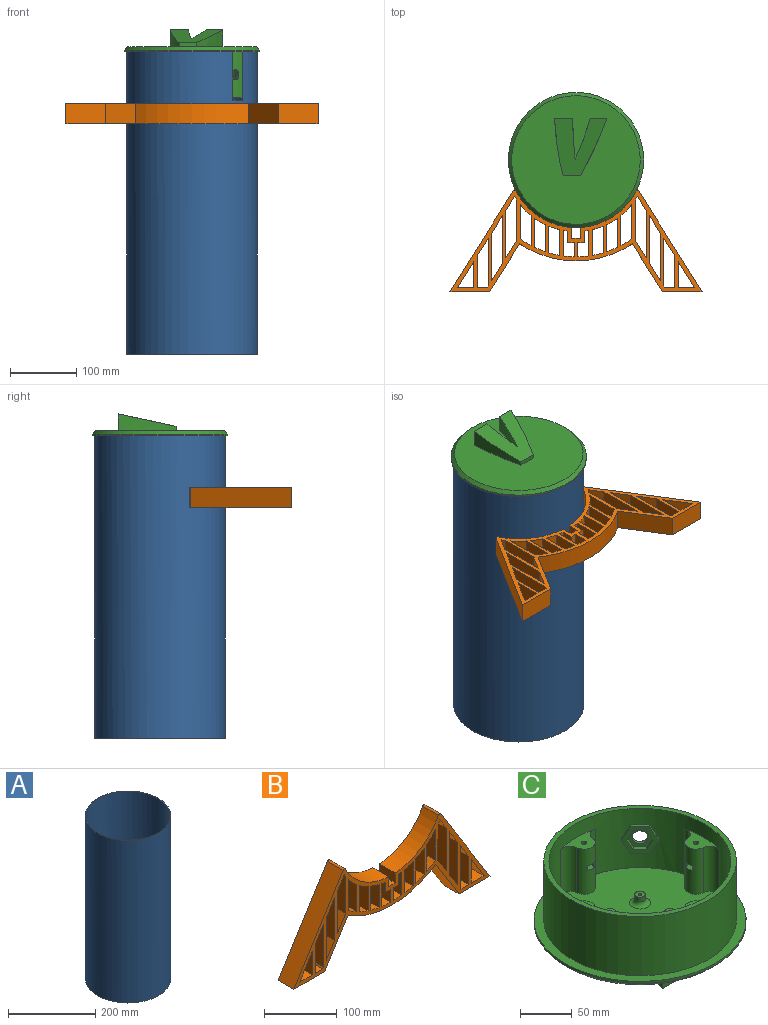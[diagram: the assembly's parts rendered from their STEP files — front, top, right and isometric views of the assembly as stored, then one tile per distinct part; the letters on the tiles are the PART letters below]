
ASSEMBLY  parts=3 mates=3
PART A: 7 faces, bbox 196.9x196.9x457.2 mm
  f0: cylinder r=96.84mm len=457.2mm, axis (0,0,-1), area 276538mm2, adj f2,f3,f4,f5,f6
  f1: cylinder r=98.42mm len=457.2mm, axis (0,0,-1), area 281098.5mm2, adj f2,f3,f4,f5,f6
  f2: plane 196.85x196.85mm, normal (0,0,1), area 938.3mm2, adj f0,f1,f5,f6
  f3: plane 196.85x196.85mm, normal (0,0,-1), area 973.8mm2, adj f0,f1
  f4: plane 16.94x16.94mm, normal (0,0,1), area 35.6mm2, adj f0,f1,f5,f6
  f5: plane 73.41x1.13mm, normal (-0.71,-0.71,0), area 117.3mm2, adj f0,f1,f2,f4
  f6: plane 73.41x1.13mm, normal (0.71,0.71,0), area 117.3mm2, adj f0,f1,f2,f4
PART B: 86 faces, bbox 381x30.5x153.5 mm
  f0: plane 381x153.53mm, normal (0,1,0), area 10608.3mm2, adj f2,f3,f4,f5,f6,f7,f8,f9
  f1: plane 381x153.53mm, normal (0,-1,0), area 10608.3mm2, adj f2,f3,f4,f5,f6,f7,f8,f9
  f2: cylinder r=101.6mm len=83.99mm, axis (0,-1,0), area 3199.2mm2, adj f0,f1,f12,f14
  f3: plane 60x30.48mm, normal (0,0,-1), area 1828.8mm2, adj f0,f1,f4,f10
  f4: plane 72.22x45.39mm, normal (0.85,0,-0.53), area 2599.8mm2, adj f0,f1,f3,f5
  f5: cylinder r=152.4mm len=170.22mm, axis (0,-1,0), area 5505mm2, adj f0,f1,f4,f6
  f6: plane 72.22x45.39mm, normal (-0.85,0,-0.53), area 2599.8mm2, adj f0,f1,f5,f7
  f7: plane 60x30.48mm, normal (0,0,-1), area 1828.8mm2, adj f0,f1,f6,f8
  f8: plane 152.34x95.75mm, normal (0.85,0,0.53), area 5484.4mm2, adj f0,f1,f7,f11
  f9: cylinder r=101.6mm len=83.99mm, axis (0,-1,0), area 3199.2mm2, adj f0,f1,f11,f13
  f10: plane 152.34x95.75mm, normal (-0.85,0,0.53), area 5484.4mm2, adj f0,f1,f3,f12
  f11: cylinder r=2.54mm len=30.48mm, axis (0,-1,0), area 163mm2, adj f0,f1,f8,f9
  f12: cylinder r=2.54mm len=30.48mm, axis (0,-1,0), area 163mm2, adj f0,f1,f2,f10
  f13: plane 30.48x16.81mm, normal (-1,0,0), area 512.3mm2, adj f0,f1,f9,f15
  f14: plane 30.48x16.81mm, normal (1,0,0), area 512.3mm2, adj f0,f1,f2,f15
  f15: plane 30.48x12.7mm, normal (0,0,1), area 387.1mm2, adj f0,f1,f13,f14
  f16: plane 30.48x26.27mm, normal (0.85,0,0.53), area 945.7mm2, adj f0,f1,f17,f19
  f17: plane 71.6x30.48mm, normal (-1,0,0), area 2182.4mm2, adj f0,f1,f16,f18
  f18: plane 30.48x26.27mm, normal (-0.85,0,-0.53), area 945.7mm2, adj f0,f1,f17,f19
  f19: plane 71.6x30.48mm, normal (1,0,0), area 2182.4mm2, adj f0,f1,f16,f18
  f20: plane 39.42x30.48mm, normal (1,0,0), area 1201.6mm2, adj f0,f1,f21,f22
  f21: plane 30.48x24.78mm, normal (0,0,1), area 755.2mm2, adj f0,f1,f20,f22
  f22: plane 39.42x30.48mm, normal (-0.85,0,-0.53), area 1419.2mm2, adj f0,f1,f20,f21
  f23: plane 47.5x30.48mm, normal (-1,0,0), area 1447.9mm2, adj f0,f1,f24,f27
  f24: plane 30.48x26.27mm, normal (-0.85,0,-0.53), area 945.7mm2, adj f0,f1,f23,f25
  f25: plane 71.6x30.48mm, normal (1,0,0), area 2182.4mm2, adj f0,f1,f24,f26
  f26: plane 30.48x2.17mm, normal (0.85,0,0.53), area 78.2mm2, adj f0,f1,f25,f27
  f27: plane 30.48x15.14mm, normal (0,0,1), area 461.6mm2, adj f0,f1,f23,f26
  f28: plane 61x30.48mm, normal (1,0,0), area 1859.2mm2, adj f0,f1,f29,f32
  f29: plane 30.48x26.27mm, normal (0.85,0,0.53), area 945.7mm2, adj f0,f1,f28,f30
  f30: plane 71.6x30.48mm, normal (-1,0,0), area 2182.4mm2, adj f0,f1,f29,f31
  f31: plane 30.48x20.95mm, normal (-0.85,0,-0.53), area 754mm2, adj f0,f1,f30,f32
  f32: cylinder r=107.95mm len=30.48mm, axis (0,-1,0), area 190.5mm2, adj f0,f1,f28,f31
  f33: cylinder r=146.05mm len=30.48mm, axis (0,-1,0), area 590.6mm2, adj f0,f1,f34,f36
  f34: plane 51.88x30.48mm, normal (-1,0,0), area 1581.3mm2, adj f0,f1,f33,f35
  f35: cylinder r=107.95mm len=30.48mm, axis (0,-1,0), area 715.4mm2, adj f0,f1,f34,f36
  f36: plane 45.38x30.48mm, normal (1,0,0), area 1383.1mm2, adj f0,f1,f33,f35
  f37: plane 44.05x30.48mm, normal (-1,0,0), area 1342.8mm2, adj f0,f1,f38,f40
  f38: cylinder r=107.95mm len=30.48mm, axis (0,-1,0), area 584.7mm2, adj f0,f1,f37,f39
  f39: plane 41x30.48mm, normal (1,0,0), area 1249.6mm2, adj f0,f1,f38,f40
  f40: cylinder r=146.05mm len=30.48mm, axis (0,-1,0), area 543mm2, adj f0,f1,f37,f39
  f41: cylinder r=146.05mm len=30.48mm, axis (0,-1,0), area 516.9mm2, adj f0,f1,f42,f44
  f42: plane 40.34x30.48mm, normal (-1,0,0), area 1229.6mm2, adj f0,f1,f41,f43
  f43: cylinder r=107.95mm len=30.48mm, axis (0,-1,0), area 529.2mm2, adj f0,f1,f42,f44
  f44: plane 38.86x30.48mm, normal (1,0,0), area 1184.4mm2, adj f0,f1,f41,f43
  f45: plane 38.57x30.48mm, normal (-1,0,0), area 1175.7mm2, adj f0,f1,f46,f50
  f46: cylinder r=107.95mm len=30.48mm, axis (0,-1,0), area 213.2mm2, adj f0,f1,f45,f47
  f47: plane 30.48x17.36mm, normal (1,0,0), area 529.1mm2, adj f0,f1,f46,f48
  f48: plane 30.48x10.16mm, normal (0,0,-1), area 309.7mm2, adj f0,f1,f47,f49
  f49: plane 30.48x21.47mm, normal (1,0,0), area 654.4mm2, adj f0,f1,f48,f50
  f50: cylinder r=146.05mm len=30.48mm, axis (0,-1,0), area 522.2mm2, adj f0,f1,f45,f49
  f51: cylinder r=107.95mm len=30.48mm, axis (0,-1,0), area 213.2mm2, adj f0,f1,f52,f56
  f52: plane 38.57x30.48mm, normal (1,0,0), area 1175.7mm2, adj f0,f1,f51,f53
  f53: cylinder r=146.05mm len=30.48mm, axis (0,-1,0), area 522.2mm2, adj f0,f1,f52,f54
  f54: plane 30.48x21.47mm, normal (-1,0,0), area 654.4mm2, adj f0,f1,f53,f55
  f55: plane 30.48x10.16mm, normal (0,0,-1), area 309.7mm2, adj f0,f1,f54,f56
  f56: plane 30.48x17.36mm, normal (-1,0,0), area 529.1mm2, adj f0,f1,f51,f55
  f57: cylinder r=107.95mm len=30.48mm, axis (0,-1,0), area 529.2mm2, adj f0,f1,f58,f60
  f58: plane 40.34x30.48mm, normal (1,0,0), area 1229.6mm2, adj f0,f1,f57,f59
  f59: cylinder r=146.05mm len=30.48mm, axis (0,-1,0), area 516.9mm2, adj f0,f1,f58,f60
  f60: plane 38.86x30.48mm, normal (-1,0,0), area 1184.4mm2, adj f0,f1,f57,f59
  f61: plane 44.05x30.48mm, normal (1,0,0), area 1342.8mm2, adj f0,f1,f62,f64
  f62: cylinder r=146.05mm len=30.48mm, axis (0,-1,0), area 543mm2, adj f0,f1,f61,f63
  f63: plane 41x30.48mm, normal (-1,0,0), area 1249.6mm2, adj f0,f1,f62,f64
  f64: cylinder r=107.95mm len=30.48mm, axis (0,-1,0), area 584.7mm2, adj f0,f1,f61,f63
  f65: cylinder r=146.05mm len=30.48mm, axis (0,-1,0), area 590.6mm2, adj f0,f1,f66,f68
  f66: plane 45.38x30.48mm, normal (-1,0,0), area 1383.1mm2, adj f0,f1,f65,f67
  f67: cylinder r=107.95mm len=30.48mm, axis (0,-1,0), area 715.4mm2, adj f0,f1,f66,f68
  f68: plane 51.88x30.48mm, normal (1,0,0), area 1581.3mm2, adj f0,f1,f65,f67
  f69: plane 30.48x26.27mm, normal (-0.85,0,0.53), area 945.7mm2, adj f0,f1,f70,f73
  f70: plane 61x30.48mm, normal (-1,0,0), area 1859.2mm2, adj f0,f1,f69,f71
  f71: cylinder r=107.95mm len=30.48mm, axis (0,-1,0), area 190.5mm2, adj f0,f1,f70,f72
  f72: plane 30.48x20.95mm, normal (0.85,0,-0.53), area 754mm2, adj f0,f1,f71,f73
  f73: plane 71.6x30.48mm, normal (1,0,0), area 2182.4mm2, adj f0,f1,f69,f72
  f74: plane 30.48x26.27mm, normal (0.85,0,-0.53), area 945.7mm2, adj f0,f1,f75,f77
  f75: plane 71.6x30.48mm, normal (1,0,0), area 2182.4mm2, adj f0,f1,f74,f76
  f76: plane 30.48x26.27mm, normal (-0.85,0,0.53), area 945.7mm2, adj f0,f1,f75,f77
  f77: plane 71.6x30.48mm, normal (-1,0,0), area 2182.4mm2, adj f0,f1,f74,f76
  f78: plane 30.48x15.14mm, normal (0,0,1), area 461.6mm2, adj f0,f1,f79,f82
  f79: plane 30.48x2.17mm, normal (-0.85,0,0.53), area 78.2mm2, adj f0,f1,f78,f80
  f80: plane 71.6x30.48mm, normal (-1,0,0), area 2182.4mm2, adj f0,f1,f79,f81
  f81: plane 30.48x26.27mm, normal (0.85,0,-0.53), area 945.7mm2, adj f0,f1,f80,f82
  f82: plane 47.5x30.48mm, normal (1,0,0), area 1447.9mm2, adj f0,f1,f78,f81
  f83: plane 39.42x30.48mm, normal (0.85,0,-0.53), area 1419.2mm2, adj f0,f1,f84,f85
  f84: plane 30.48x24.78mm, normal (0,0,1), area 755.2mm2, adj f0,f1,f83,f85
  f85: plane 39.42x30.48mm, normal (-1,0,0), area 1201.6mm2, adj f0,f1,f83,f84
PART C: 115 faces, bbox 204.5x204.5x102.9 mm
  f0: cylinder r=87.79mm len=175.58mm, axis (0,0,-1), area 27432.1mm2, adj f7,f40,f42,f44,f46,f48,f89,f90
  f1: cylinder r=560.8mm len=87.22mm, axis (0,0,1), area 1511.2mm2, adj f2,f6,f98,f99
  f2: plane 26.41x6.35mm, normal (0,1,0), area 167.7mm2, adj f1,f3,f6,f99
  f3: cylinder r=440.97mm len=87.22mm, axis (0,0,1), area 1398mm2, adj f2,f6,f97,f99
  f4: cylinder r=576.44mm len=61.68mm, axis (0,0,1), area 1154.1mm2, adj f5,f6,f97,f99
  f5: cylinder r=408.24mm len=61.68mm, axis (0,0,1), area 1223.8mm2, adj f4,f6,f98,f99
  f6: plane 194.31x194.31mm, normal (0,0,-1), area 25705.9mm2, adj f1,f2,f3,f4,f5,f49,f97,f98
  f7: plane 169.84x169.84mm, normal (0,0,1), area 20911.6mm2, adj f0,f8,f9,f10,f11,f12,f13,f14
  f8: cylinder r=10.8mm len=53.34mm, axis (0,0,-1), area 1666.1mm2, adj f7,f9,f10,f40,f55,f69,f87,f88
  f9: plane 53.34x0.04mm, normal (0.07,1,0), area 2.4mm2, adj f7,f8,f40,f93
  f10: plane 53.34x0.04mm, normal (0.07,-1,0), area 2.4mm2, adj f7,f8,f40,f94
  f11: cylinder r=10.8mm len=53.34mm, axis (0,0,-1), area 1666.1mm2, adj f7,f12,f13,f42,f67,f72,f81,f82
  f12: plane 53.34x0.04mm, normal (-1,0.07,0), area 2.4mm2, adj f7,f11,f42,f90
  f13: plane 53.34x0.04mm, normal (1,0.07,0), area 2.4mm2, adj f7,f11,f42,f89
  f14: cylinder r=10.8mm len=53.34mm, axis (0,0,-1), area 1666.1mm2, adj f7,f15,f16,f44,f63,f71,f83,f84
  f15: plane 53.34x0.04mm, normal (-0.07,-1,0), area 2.4mm2, adj f7,f14,f44,f92
  f16: plane 53.34x0.04mm, normal (-0.07,1,0), area 2.4mm2, adj f7,f14,f44,f91
  f17: cylinder r=10.8mm len=53.34mm, axis (0,0,-1), area 1666.1mm2, adj f7,f18,f19,f46,f59,f70,f85,f86
  f18: plane 53.34x0.04mm, normal (1,-0.07,0), area 2.4mm2, adj f7,f17,f46,f96
  f19: plane 53.34x0.04mm, normal (-1,-0.07,0), area 2.4mm2, adj f7,f17,f46,f95
  f20: cylinder r=1.81mm len=10.16mm, axis (0,0,-1), area 115.5mm2, adj f22,f23
  f21: cylinder r=5.08mm len=10.16mm, axis (0,0,-1), area 162.1mm2, adj f22,f39
  f22: plane 10.16x10.16mm, normal (0,0,1), area 70.8mm2, adj f20,f21
  f23: plane 3.62x3.62mm, normal (0,0,1), area 10.3mm2, adj f20
  f24: cylinder r=1.81mm len=10.16mm, axis (0,0,-1), area 115.5mm2, adj f26,f27
  f25: cylinder r=5.08mm len=10.16mm, axis (0,0,-1), area 162.1mm2, adj f26,f38
  f26: plane 10.16x10.16mm, normal (0,0,1), area 70.8mm2, adj f24,f25
  f27: plane 3.62x3.62mm, normal (0,0,1), area 10.3mm2, adj f24
  f28: cylinder r=1.81mm len=10.16mm, axis (0,0,-1), area 115.5mm2, adj f30,f31
  f29: cylinder r=5.08mm len=10.16mm, axis (0,0,-1), area 162.1mm2, adj f30,f37
  f30: plane 10.16x10.16mm, normal (0,0,1), area 70.8mm2, adj f28,f29
  f31: plane 3.62x3.62mm, normal (0,0,1), area 10.3mm2, adj f28
  f32: cylinder r=1.81mm len=10.16mm, axis (0,0,-1), area 115.5mm2, adj f34,f35
  f33: cylinder r=5.08mm len=10.16mm, axis (0,0,-1), area 162.1mm2, adj f34,f36
  f34: plane 10.16x10.16mm, normal (0,0,1), area 70.8mm2, adj f32,f33
  f35: plane 3.62x3.62mm, normal (0,0,1), area 10.3mm2, adj f32
  f36: torus R=10.16mm, axis (0,0,1), area 347.3mm2, adj f7,f33
  f37: torus R=10.16mm, axis (0,0,1), area 347.3mm2, adj f7,f29
  f38: torus R=10.16mm, axis (0,0,1), area 347.3mm2, adj f7,f25
  f39: torus R=10.16mm, axis (0,0,1), area 347.3mm2, adj f7,f21
  f40: plane 47.3x22.39mm, normal (0,0,1), area 478.4mm2, adj f0,f8,f9,f10,f41,f93,f94
  f41: cylinder r=2.67mm len=20mm, axis (0,0,-1), area 335.2mm2, adj f40,f55
  f42: plane 47.3x22.39mm, normal (0,0,1), area 478.4mm2, adj f0,f11,f12,f13,f43,f89,f90
  f43: cylinder r=2.67mm len=20mm, axis (0,0,-1), area 335.2mm2, adj f42,f67
  f44: plane 47.3x22.39mm, normal (0,0,1), area 478.4mm2, adj f0,f14,f15,f16,f45,f91,f92
  f45: cylinder r=2.67mm len=20mm, axis (0,0,-1), area 335.2mm2, adj f44,f63
  f46: plane 47.3x22.39mm, normal (0,0,1), area 478.4mm2, adj f0,f17,f18,f19,f47,f95,f96
  f47: cylinder r=2.67mm len=20mm, axis (0,0,-1), area 335.2mm2, adj f46,f59
  f48: plane 185.74x185.74mm, normal (0,0,1), area 2883.2mm2, adj f0,f52
  f49: cone r=102.23mm half-angle=45deg, axis (0,0,1), area 4500.2mm2, adj f6,f50
  f50: cylinder r=102.23mm len=204.47mm, axis (0,0,-1), area 1631.6mm2, adj f49,f51
  f51: plane 204.47x204.47mm, normal (0,0,1), area 5740.9mm2, adj f50,f52
  f52: cylinder r=92.87mm len=185.74mm, axis (0,0,-1), area 40574.5mm2, adj f48,f51,f113
  f53: plane 13.04x5.4mm, normal (0,1,0), area 70.4mm2, adj f55,f56,f69,f88
  f54: plane 13.04x5.4mm, normal (0,-1,0), area 70.4mm2, adj f55,f56,f69,f87
  f55: plane 15.28x11.04mm, normal (0,0,-1), area 107mm2, adj f8,f41,f53,f54,f56,f87,f88
  f56: plane 8.51x5.4mm, normal (1,0,0), area 45.9mm2, adj f53,f54,f55,f69
  f57: plane 13.04x5.4mm, normal (-1,0,0), area 70.4mm2, adj f59,f60,f70,f86
  f58: plane 13.04x5.4mm, normal (1,0,0), area 70.4mm2, adj f59,f60,f70,f85
  f59: plane 15.28x11.04mm, normal (0,0,-1), area 107mm2, adj f17,f47,f57,f58,f60,f85,f86
  f60: plane 8.51x5.4mm, normal (0,-1,0), area 45.9mm2, adj f57,f58,f59,f70
  f61: plane 13.04x5.4mm, normal (0,1,0), area 70.4mm2, adj f63,f64,f71,f84
  f62: plane 13.04x5.4mm, normal (0,-1,0), area 70.4mm2, adj f63,f64,f71,f83
  f63: plane 15.28x11.04mm, normal (0,0,-1), area 107mm2, adj f14,f45,f61,f62,f64,f83,f84
  f64: plane 8.51x5.4mm, normal (-1,0,0), area 45.9mm2, adj f61,f62,f63,f71
  f65: plane 13.04x5.4mm, normal (1,0,0), area 70.4mm2, adj f67,f68,f72,f82
  f66: plane 13.04x5.4mm, normal (-1,0,0), area 70.4mm2, adj f67,f68,f72,f81
  f67: plane 15.28x11.04mm, normal (0,0,-1), area 107mm2, adj f11,f43,f65,f66,f68,f81,f82
  f68: plane 8.51x5.4mm, normal (0,1,0), area 45.9mm2, adj f65,f66,f67,f72
  f69: plane 15.28x11.04mm, normal (0,0,1), area 107mm2, adj f8,f53,f54,f56,f79,f87,f88
  f70: plane 15.28x11.04mm, normal (0,0,1), area 107mm2, adj f17,f57,f58,f60,f77,f85,f86
  f71: plane 15.28x11.04mm, normal (0,0,1), area 107mm2, adj f14,f61,f62,f64,f75,f83,f84
  f72: plane 15.28x11.04mm, normal (0,0,1), area 107mm2, adj f11,f65,f66,f68,f73,f81,f82
  f73: cylinder r=2.67mm len=12.7mm, axis (0,0,1), area 212.8mm2, adj f72,f74
  f74: plane 5.33x5.33mm, normal (0,0,1), area 22.3mm2, adj f73
  f75: cylinder r=2.67mm len=12.7mm, axis (0,0,1), area 212.8mm2, adj f71,f76
  f76: plane 5.33x5.33mm, normal (0,0,1), area 22.3mm2, adj f75
  f77: cylinder r=2.67mm len=12.7mm, axis (0,0,1), area 212.8mm2, adj f70,f78
  f78: plane 5.33x5.33mm, normal (0,0,1), area 22.3mm2, adj f77
  f79: cylinder r=2.67mm len=12.7mm, axis (0,0,1), area 212.8mm2, adj f69,f80
  f80: plane 5.33x5.33mm, normal (0,0,1), area 22.3mm2, adj f79
  f81: plane 5.4x1.27mm, normal (-0.49,0.87,0), area 7.9mm2, adj f11,f66,f67,f72
  f82: plane 5.4x1.27mm, normal (0.49,0.87,0), area 7.9mm2, adj f11,f65,f67,f72
  f83: plane 5.4x1.27mm, normal (-0.87,-0.49,0), area 7.9mm2, adj f14,f62,f63,f71
  f84: plane 5.4x1.27mm, normal (-0.87,0.49,0), area 7.9mm2, adj f14,f61,f63,f71
  f85: plane 5.4x1.27mm, normal (0.49,-0.87,0), area 7.9mm2, adj f17,f58,f59,f70
  f86: plane 5.4x1.27mm, normal (-0.49,-0.87,0), area 7.9mm2, adj f17,f57,f59,f70
  f87: plane 5.4x1.27mm, normal (0.87,-0.49,0), area 7.9mm2, adj f8,f54,f55,f69
  f88: plane 5.4x1.27mm, normal (0.87,0.49,0), area 7.9mm2, adj f8,f53,f55,f69
  f89: cylinder r=10.16mm len=53.34mm, axis (0,0,-1), area 960.6mm2, adj f0,f7,f13,f42
  f90: cylinder r=10.16mm len=53.34mm, axis (0,0,-1), area 960.6mm2, adj f0,f7,f12,f42
  f91: cylinder r=10.16mm len=53.34mm, axis (0,0,-1), area 960.6mm2, adj f0,f7,f16,f44
  f92: cylinder r=10.16mm len=53.34mm, axis (0,0,-1), area 960.6mm2, adj f0,f7,f15,f44
  f93: cylinder r=10.16mm len=53.34mm, axis (0,0,-1), area 960.6mm2, adj f0,f7,f9,f40
  f94: cylinder r=10.16mm len=53.34mm, axis (0,0,-1), area 960.6mm2, adj f0,f7,f10,f40
  f95: cylinder r=10.16mm len=53.34mm, axis (0,0,-1), area 960.6mm2, adj f0,f7,f19,f46
  f96: cylinder r=10.16mm len=53.34mm, axis (0,0,-1), area 960.6mm2, adj f0,f7,f18,f46
  f97: plane 27.43x25.4mm, normal (0,-1,0), area 696.7mm2, adj f3,f4,f6,f99
  f98: plane 25.4x25.04mm, normal (0,-1,0), area 636mm2, adj f1,f5,f6,f99
  f99: plane 87.24x79.08mm, normal (0,0.21,-0.98), area 4040.9mm2, adj f1,f2,f3,f4,f5,f97,f98
  f100: plane 15.49x15.49mm, normal (0,0,-1), area 71.3mm2, adj f0,f101,f104,f114
  f101: plane 15.94x9.07mm, normal (-0.61,0.61,-0.5), area 53.6mm2, adj f0,f100,f102,f114
  f102: plane 15.94x9.07mm, normal (-0.61,0.61,0.5), area 53.6mm2, adj f0,f101,f103,f114
  f103: plane 15.49x15.49mm, normal (0,0,1), area 71.3mm2, adj f0,f102,f105,f114
  f104: plane 15.94x9.07mm, normal (0.61,-0.61,-0.5), area 53.6mm2, adj f0,f100,f105,f114
  f105: plane 15.94x9.07mm, normal (0.61,-0.61,0.5), area 53.6mm2, adj f0,f103,f104,f114
  f106: plane 11.18x8.15mm, normal (0.61,-0.61,0.5), area 65.6mm2, adj f107,f111,f112,f114
  f107: plane 12.72x12.72mm, normal (0,0,1), area 65.6mm2, adj f106,f108,f112,f114
  f108: plane 11.18x8.15mm, normal (-0.61,0.61,0.5), area 65.6mm2, adj f107,f109,f112,f114
  f109: plane 11.18x8.15mm, normal (-0.61,0.61,-0.5), area 65.6mm2, adj f108,f110,f112,f114
  f110: plane 12.72x12.72mm, normal (0,0,-1), area 65.6mm2, adj f109,f111,f112,f114
  f111: plane 11.18x8.15mm, normal (0.61,-0.61,-0.5), area 65.6mm2, adj f106,f110,f112,f114
  f112: plane 22.35x18.25mm, normal (-0.71,-0.71,0), area 250.3mm2, adj f106,f107,f108,f109,f110,f111,f113
  f113: cylinder r=7.62mm len=15.24mm, axis (-0.71,-0.71,0), area 186.4mm2, adj f52,f112
  f114: plane 31.75x25.92mm, normal (-0.71,-0.71,0), area 440.3mm2, adj f100,f101,f102,f103,f104,f105,f106,f107
PLACE A t=(-180.94,33.46,-27.89)mm
PLACE B rot(axis=(-1,0,0),90deg) t=(-180.94,-50.04,350.57)mm
PLACE C rot(axis=(1,0,0),180deg) t=(-180.94,33.46,436.93)mm
MATE cylindrical C.f52 <-> A.f0  axis (0,0,1) through (-180.94,33.46,394.39)mm
MATE planar C.f49 <-> A.f2  axis (0,0,-1) through (-180.94,33.46,429.31)mm
MATE cylindrical B.f2 <-> A.f1  axis (0,0,1) through (-180.94,33.46,320.09)mm
